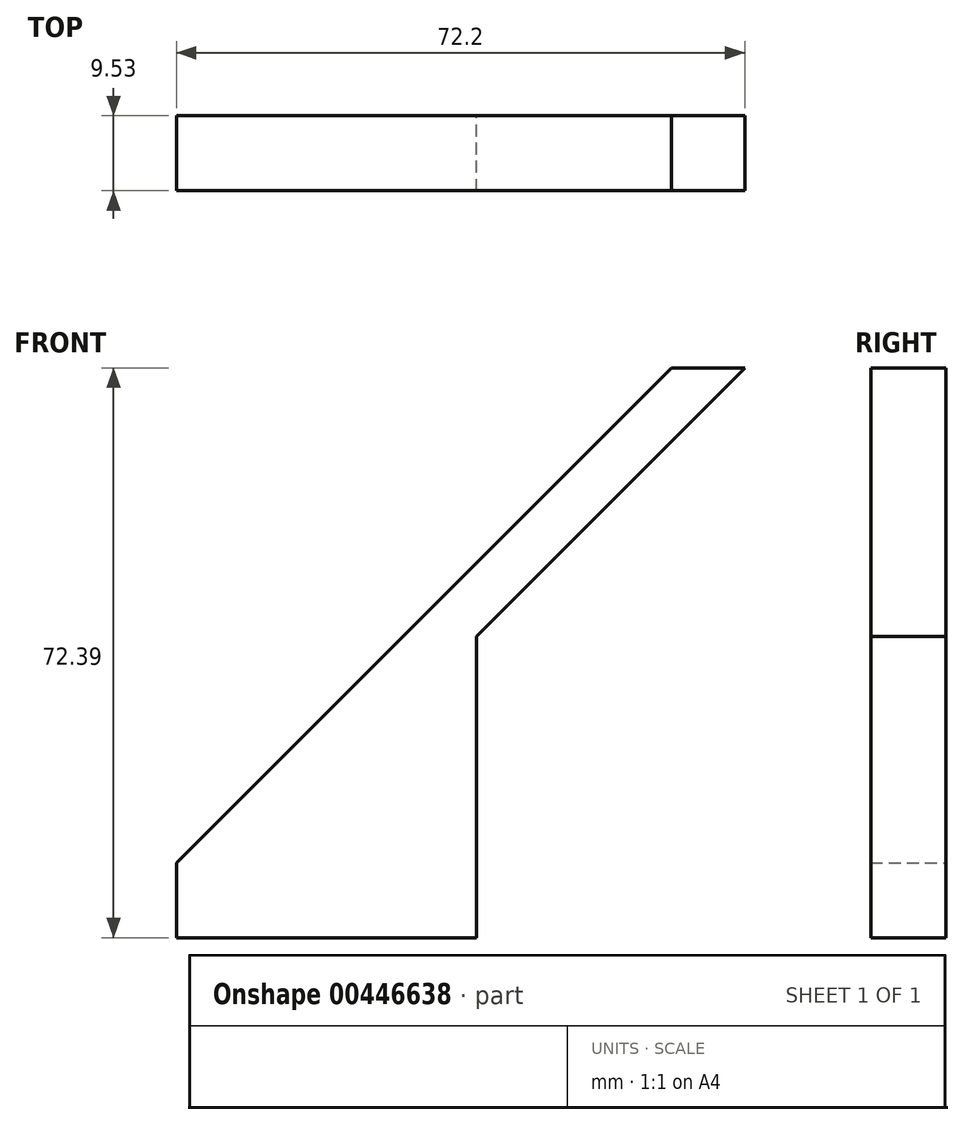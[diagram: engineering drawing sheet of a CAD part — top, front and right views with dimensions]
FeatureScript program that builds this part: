
annotation { "Feature Type Name" : "Feature", "Feature Type Description" : "" }
export const myFeature = defineFeature(function(context is Context, id is Id, definition is map)
    precondition{}
    {
        {
            var Q0;
            Q0=qCreatedBy(makeId("Front.planeOp"),FACE);
            var sketch = newSketch(context, id + "F0", { "sketchPlane" : qUnion([Q0])});
            skLineSegment(sketch, "E0", {"start": v(0, 0) * mm, "end": v(62.86, 62.86) * mm});
            skLineSegment(sketch, "E1", {"start": v(9.34, 0) * mm, "end": v(72.2, 62.86) * mm});
            skLineSegment(sketch, "E2", {"start": v(72.2, 62.86) * mm, "end": v(62.86, 62.86) * mm});
            skLineSegment(sketch, "E3.bottom", {"start": v(0, 0) * mm, "end": v(38.1, 0) * mm});
            skLineSegment(sketch, "E3.top", {"start": v(0, -9.53) * mm, "end": v(38.1, -9.53) * mm});
            skLineSegment(sketch, "E3.left", {"start": v(0, 0) * mm, "end": v(0, -9.53) * mm});
            skLineSegment(sketch, "E3.right", {"start": v(38.1, 0) * mm, "end": v(38.1, -9.53) * mm});
            skLineSegment(sketch, "E4", {"start": v(38.1, 0) * mm, "end": v(38.1, 28.76) * mm});
            skSolve(sketch);
        }
        {
            var Q0;
            Q0 = qSketchRegion(id + "F0", true);
            extrude(context, id + "F1", {"entities" : qUnion([Q0]), "depth" : 9.52 * mm});
        }
    });
